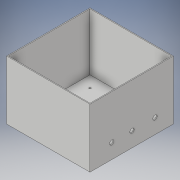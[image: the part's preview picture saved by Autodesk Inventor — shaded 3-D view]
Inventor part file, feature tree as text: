
AUTODESK INVENTOR PART (.ipt)
format: ipt  version: 2018 (Build 220112000, 112)  size: 154,624 bytes
history: native  units: in
note: dims shown in document units (in); Inventor stores cm internally (conversion verified against a paired STEP export)
features: extrude x6, sketch x6
ambient origin geometry x8: Origin, YZ Plane, XZ Plane, XY Plane, X Axis, Y Axis, Z Axis, Center Point
bodies: Solid1 (feature_tree)
feature tree (12):
  extrude  "Extrusion1"  Depth=4.76in
  extrude  "Extrusion2"  Depth=4.66in
  extrude  "Extrusion3"  Depth=3.26in TaperAngle=0.0deg
  extrude  "Extrusion4"  Depth=0.164in
  extrude  "Extrusion5"  Depth=2.598in
  extrude  "Extrusion6"  Depth=0.118in
  sketch  "Sketch1"  dims[d0=4.76in d1=4.76in]
  sketch  "Sketch2"  dims[d2=0.1in d3=0.0in d4=4.66in]
  sketch  "Sketch3"  dims[d5=4.66in d6=3.26in d7=0.0in]
  sketch  "Sketch4"  dims[d10=0.164in d11=0.164in]
  sketch  "Sketch5"  dims[d12=0.0in d13=0.0in d14=2.598in]
  sketch  "Sketch7"  dims[d15=0.787in d16=0.118in d17=0.118in d18=0.118in d19=0.118in d20=3.937in d21=3.937in d28=0.112in d29=0.112in d30=0.112in d31=0.112in d32=0.0in d33=0.0in d34=0.25in d35=1.0in d36=0.0in d43=0.0in d44=0.0in d50=0.25in d51=0.25in d52=0.25in]
